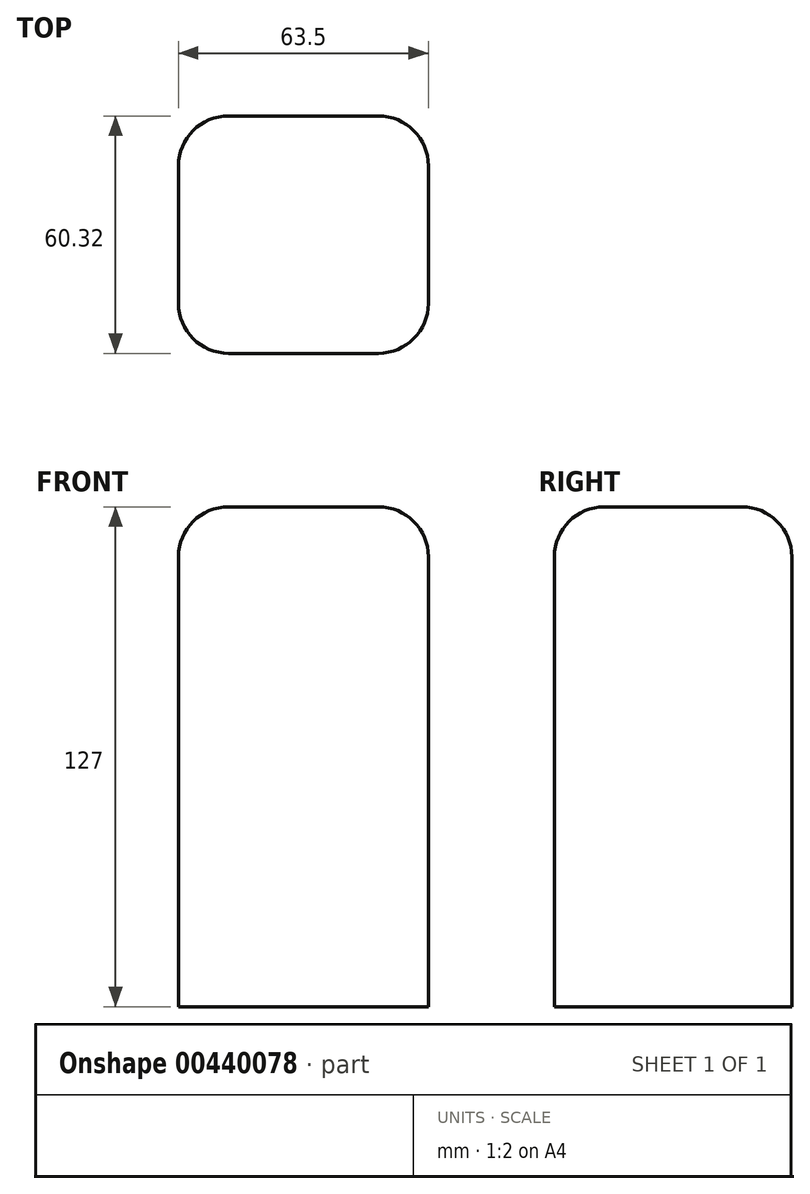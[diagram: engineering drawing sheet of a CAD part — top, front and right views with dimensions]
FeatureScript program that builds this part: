
annotation { "Feature Type Name" : "Feature", "Feature Type Description" : "" }
export const myFeature = defineFeature(function(context is Context, id is Id, definition is map)
    precondition{}
    {
        {
            var Q0;
            Q0=qCreatedBy(makeId("Front.planeOp"),FACE);
            var sketch = newSketch(context, id + "F0", { "sketchPlane" : qUnion([Q0])});
            skLineSegment(sketch, "E0.bottom", {"start": v(-31.75, -63.5) * mm, "end": v(31.75, -63.5) * mm});
            skLineSegment(sketch, "E0.top", {"start": v(-31.75, 63.5) * mm, "end": v(31.75, 63.5) * mm});
            skLineSegment(sketch, "E0.left", {"start": v(-31.75, -63.5) * mm, "end": v(-31.75, 63.5) * mm});
            skLineSegment(sketch, "E0.right", {"start": v(31.75, -63.5) * mm, "end": v(31.75, 63.5) * mm});
            skPoint(sketch, "E0.middle", {"position": v(0, 0) * mm});
            skSolve(sketch);
        }
        {
            var Q0;
            Q0=makeQuery(id+"F0.imprint","IMPRINT",FACE,{"disambiguationData":[TD([[makeQuery(id+"F0.imprint","IMPRINT",EDGE,{"derivedFrom":sQuery(id+"F0.wireOp",EDGE,"E0.bottom")}),1.0]])]});
            extrude(context, id + "F1", {"entities" : qUnion([Q0]), "endBound" : BoundingType.SYMMETRIC, "depth" : 60.32 * mm});
        }
        {
            var Q0;
            Q0=makeQuery(id+"F1.opExtrude","CAP_EDGE",EDGE,{"disambiguationData":[OSD([sQuery(id+"F0.wireOp",EDGE,"E0.right")])],"isStart":false});
            var Q1;
            Q1=makeQuery(id+"F1.opExtrude","CAP_EDGE",EDGE,{"disambiguationData":[OSD([sQuery(id+"F0.wireOp",EDGE,"E0.right")])],"isStart":true});
            var Q2;
            Q2=makeQuery(id+"F1.opExtrude","CAP_EDGE",EDGE,{"disambiguationData":[OSD([sQuery(id+"F0.wireOp",EDGE,"E0.left")])],"isStart":false});
            var Q3;
            Q3=makeQuery(id+"F1.opExtrude","CAP_EDGE",EDGE,{"disambiguationData":[OSD([sQuery(id+"F0.wireOp",EDGE,"E0.top")])],"isStart":false});
            var Q4;
            Q4=makeQuery(id+"F1.opExtrude","SWEPT_EDGE",EDGE,{"disambiguationData":[OSD([sQuery(id+"F0.wireOp",EDGE,"E0.top"),sQuery(id+"F0.wireOp",EDGE,"E0.right")])]});
            var Q5;
            Q5=makeQuery(id+"F1.opExtrude","SWEPT_FACE",FACE,{"disambiguationData":[OSD([sQuery(id+"F0.wireOp",EDGE,"E0.top")])]});
            var Q6;
            Q6=makeQuery(id+"F1.opExtrude","CAP_EDGE",EDGE,{"disambiguationData":[OSD([sQuery(id+"F0.wireOp",EDGE,"E0.top")])],"isStart":true});
            var Q7;
            Q7=makeQuery(id+"F1.opExtrude","CAP_EDGE",EDGE,{"disambiguationData":[OSD([sQuery(id+"F0.wireOp",EDGE,"E0.left")])],"isStart":true});
            fillet(context, id + "F2", {"entities" : qUnion([Q0, Q1, Q2, Q3, Q4, Q5, Q6, Q7]), "radius" : 12.7 * mm, "tangentPropagation" : true, "allowEdgeOverflow" : false});
        }
    });
